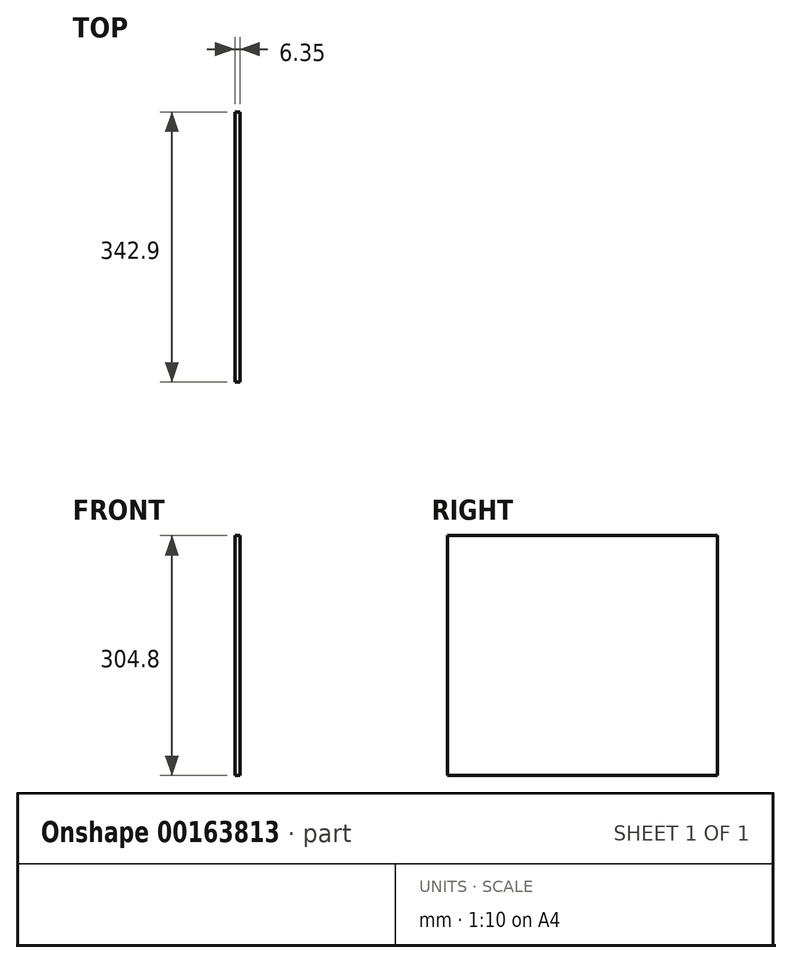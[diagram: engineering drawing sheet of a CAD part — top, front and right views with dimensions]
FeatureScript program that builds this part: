
annotation { "Feature Type Name" : "Feature", "Feature Type Description" : "" }
export const myFeature = defineFeature(function(context is Context, id is Id, definition is map)
    precondition{}
    {
        {
            var Q0;
            Q0=qCreatedBy(makeId("Right.planeOp"),FACE);
            var sketch = newSketch(context, id + "F0", { "sketchPlane" : qUnion([Q0])});
            skLineSegment(sketch, "E0.bottom", {"start": v(171.45, -152.4) * mm, "end": v(-171.45, -152.4) * mm});
            skLineSegment(sketch, "E0.top", {"start": v(171.45, 152.4) * mm, "end": v(-171.45, 152.4) * mm});
            skLineSegment(sketch, "E0.left", {"start": v(171.45, -152.4) * mm, "end": v(171.45, 152.4) * mm});
            skLineSegment(sketch, "E0.right", {"start": v(-171.45, -152.4) * mm, "end": v(-171.45, 152.4) * mm});
            skPoint(sketch, "E0.middle", {"position": v(0, 0) * mm});
            skSolve(sketch);
        }
        {
            var Q0;
            Q0=qSketchRegion(id+"F0",true);
            extrude(context, id + "F1", {"entities" : qUnion([Q0]), "depth" : 6.35 * mm});
        }
    });
